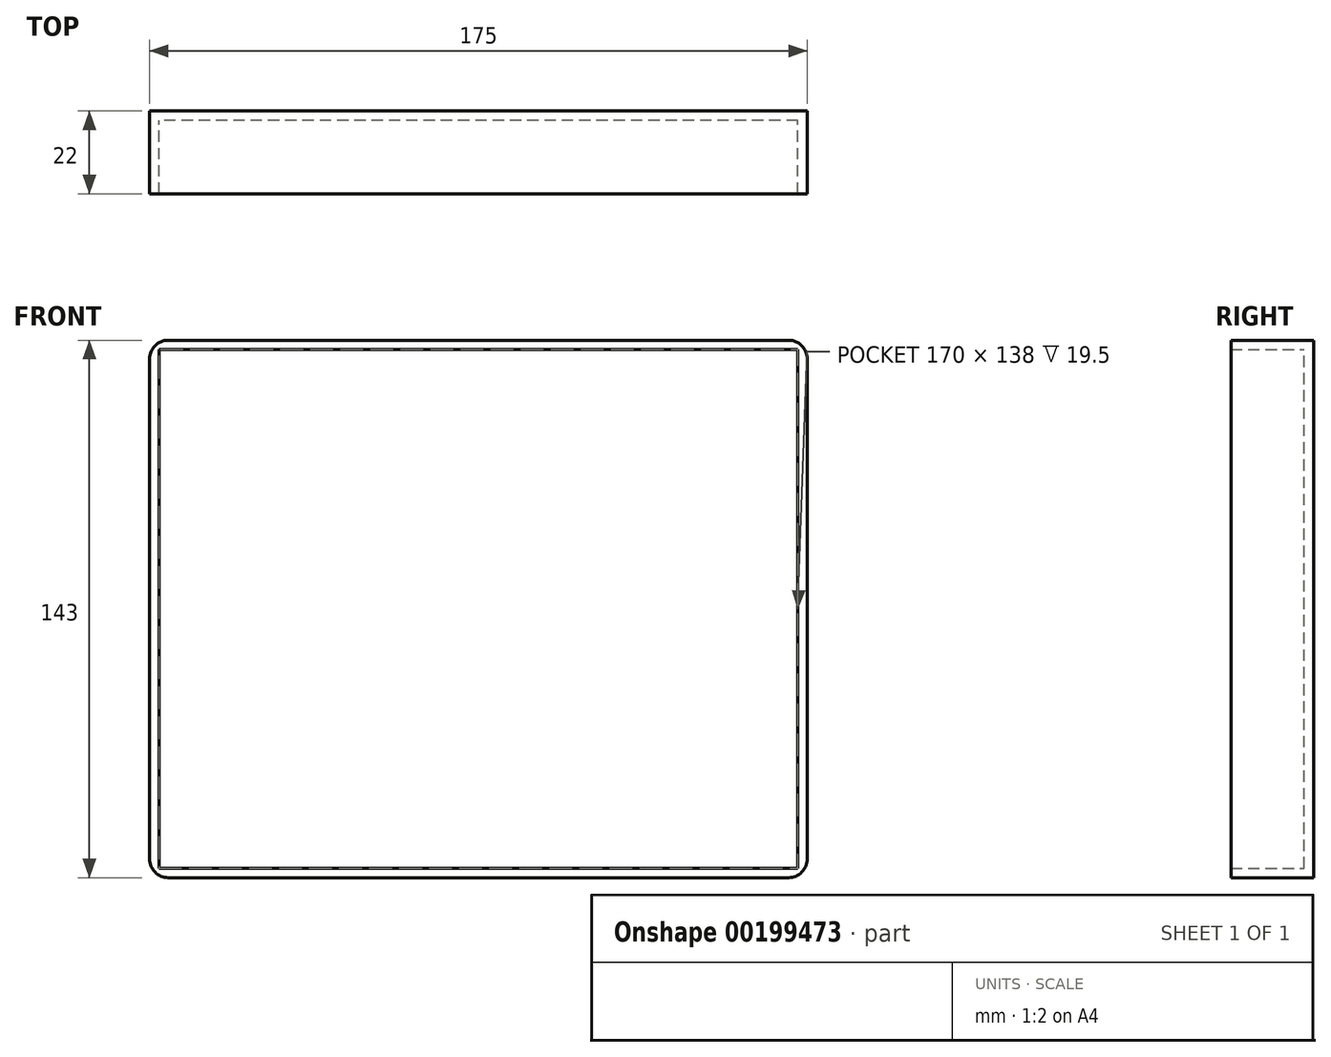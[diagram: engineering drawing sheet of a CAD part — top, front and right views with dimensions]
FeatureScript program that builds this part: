
annotation { "Feature Type Name" : "Feature", "Feature Type Description" : "" }
export const myFeature = defineFeature(function(context is Context, id is Id, definition is map)
    precondition{}
    {
        {
            var Q0;
            Q0=qCreatedBy(makeId("Front.planeOp"),FACE);
            var sketch = newSketch(context, id + "F0", { "sketchPlane" : qUnion([Q0])});
            skLineSegment(sketch, "E0.bottom", {"start": v(87.5, -71.5) * mm, "end": v(-87.5, -71.5) * mm});
            skLineSegment(sketch, "E0.top", {"start": v(87.5, 71.5) * mm, "end": v(-87.5, 71.5) * mm});
            skLineSegment(sketch, "E0.left", {"start": v(87.5, -71.5) * mm, "end": v(87.5, 71.5) * mm});
            skLineSegment(sketch, "E0.right", {"start": v(-87.5, -71.5) * mm, "end": v(-87.5, 71.5) * mm});
            skPoint(sketch, "E0.middle", {"position": v(0, 0) * mm});
            skSolve(sketch);
        }
        {
            var Q0;
            Q0 = qSketchRegion(id + "F0", true);
            extrude(context, id + "F1", {"entities" : qUnion([Q0]), "depth" : 22 * mm});
        }
        {
            var Q0;
            Q0=makeQuery(id+"F1.opExtrude","CAP_FACE",FACE,{"disambiguationData":[OSD([sQuery(id+"F0.wireOp",EDGE,"E0.bottom"),sQuery(id+"F0.wireOp",EDGE,"E0.top"),sQuery(id+"F0.wireOp",EDGE,"E0.left"),sQuery(id+"F0.wireOp",EDGE,"E0.right")])],"isStart":false});
            shell(context, id + "F2", {"entities" : qUnion([Q0]), "thickness" : 2.5 * mm});
        }
        {
            var Q0;
            Q0=makeQuery(id+"F1.opExtrude","SWEPT_EDGE",EDGE,{"disambiguationData":[OSD([sQuery(id+"F0.wireOp",EDGE,"E0.top"),sQuery(id+"F0.wireOp",EDGE,"E0.right")])]});
            var Q1;
            Q1=makeQuery(id+"F1.opExtrude","SWEPT_EDGE",EDGE,{"disambiguationData":[OSD([sQuery(id+"F0.wireOp",EDGE,"E0.bottom"),sQuery(id+"F0.wireOp",EDGE,"E0.right")])]});
            var Q2;
            Q2=makeQuery(id+"F1.opExtrude","SWEPT_EDGE",EDGE,{"disambiguationData":[OSD([sQuery(id+"F0.wireOp",EDGE,"E0.top"),sQuery(id+"F0.wireOp",EDGE,"E0.left")])]});
            var Q3;
            Q3=makeQuery(id+"F1.opExtrude","SWEPT_EDGE",EDGE,{"disambiguationData":[OSD([sQuery(id+"F0.wireOp",EDGE,"E0.bottom"),sQuery(id+"F0.wireOp",EDGE,"E0.left")])]});
            fillet(context, id + "F3", {"entities" : qUnion([Q0, Q1, Q2, Q3]), "radius" : 5 * mm, "tangentPropagation" : true, "allowEdgeOverflow" : false});
        }
    });
